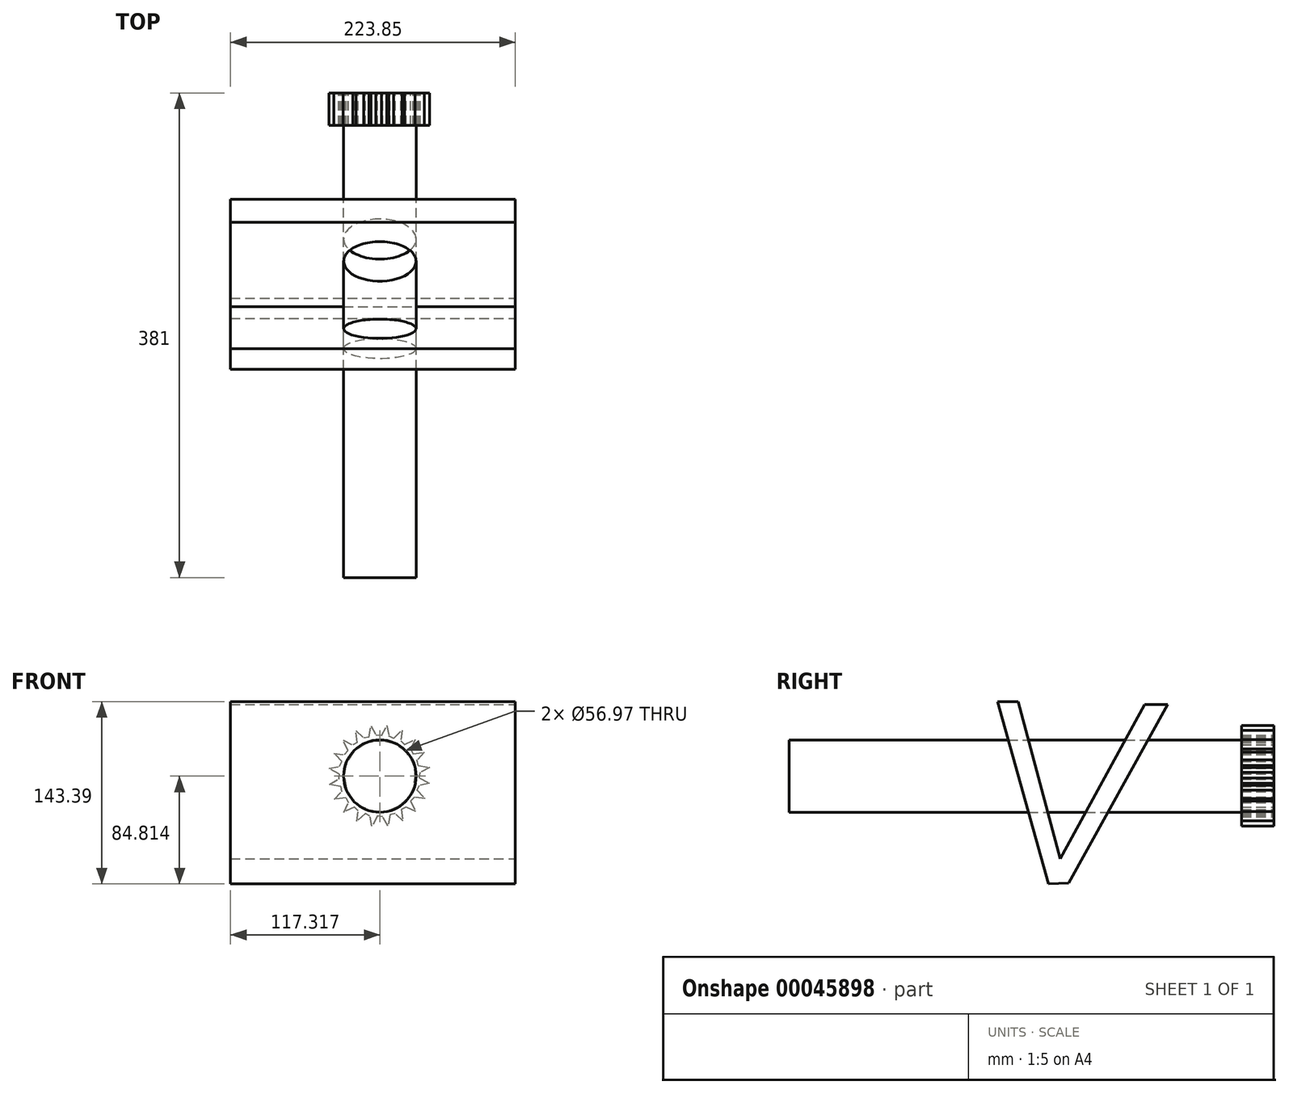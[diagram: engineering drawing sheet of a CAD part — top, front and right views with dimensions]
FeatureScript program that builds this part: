
annotation { "Feature Type Name" : "Feature", "Feature Type Description" : "" }
export const myFeature = defineFeature(function(context is Context, id is Id, definition is map)
    precondition{}
    {
        {
            var Q0;
            Q0=qCreatedBy(makeId("Front.planeOp"),FACE);
            var sketch = newSketch(context, id + "F0", { "sketchPlane" : qUnion([Q0])});
            skCircle(sketch, "E0", {"center": v(-106.53, 34.14) * mm, "radius": 28.48 * mm});
            skSolve(sketch);
        }
        {
            var Q0;
            Q0=makeQuery(id+"F0.imprint","IMPRINT",FACE,{"disambiguationData":[TD([[makeQuery(id+"F0.imprint","IMPRINT",EDGE,{"derivedFrom":sQuery(id+"F0.wireOp",EDGE,"E0")}),1.0]])]});
            extrude(context, id + "F1", {"entities" : qUnion([Q0]), "depth" : 381 * mm});
        }
        {
            var Q0;
            Q0=qCreatedBy(makeId("Right.planeOp"),FACE);
            var sketch = newSketch(context, id + "F2", { "sketchPlane" : qUnion([Q0])});
            skLineSegment(sketch, "E1", {"start": v(-83.69, 90.52) * mm, "end": v(-161.5, -50.05) * mm});
            skLineSegment(sketch, "E2", {"start": v(-83.69, 90.52) * mm, "end": v(-101.57, 90.52) * mm});
            skLineSegment(sketch, "E3", {"start": v(-101.57, 90.52) * mm, "end": v(-168.09, -30.9) * mm});
            skLineSegment(sketch, "E4", {"start": v(-168.09, -30.9) * mm, "end": v(-201.03, 92.72) * mm});
            skLineSegment(sketch, "E5", {"start": v(-201.03, 92.72) * mm, "end": v(-217.35, 92.72) * mm});
            skLineSegment(sketch, "E6", {"start": v(-217.35, 92.72) * mm, "end": v(-177.19, -50.67) * mm});
            skLineSegment(sketch, "E7", {"start": v(-177.19, -50.67) * mm, "end": v(-161.5, -50.05) * mm});
            skSolve(sketch);
        }
        {
            var Q0;
            Q0 = qSketchRegion(id + "F2", true);
            extrude(context, id + "F3", {"entities" : qUnion([Q0]), "oppositeDirection" : true, "depth" : 223.85 * mm});
        }
        {
            var Q0;
            Q0=makeQuery(id+"F1.opExtrude","SWEPT_BODY",BODY,{"disambiguationData":[OSD([sQuery(id+"F0.wireOp",EDGE,"E0")])]});
            var Q1;
            Q1=makeQuery(id+"F3.opExtrude","SWEPT_BODY",BODY,{"disambiguationData":[OSD([sQuery(id+"F2.wireOp",EDGE,"E1"),sQuery(id+"F2.wireOp",EDGE,"E2"),sQuery(id+"F2.wireOp",EDGE,"E3"),sQuery(id+"F2.wireOp",EDGE,"E4"),sQuery(id+"F2.wireOp",EDGE,"E5"),sQuery(id+"F2.wireOp",EDGE,"E6"),sQuery(id+"F2.wireOp",EDGE,"E7")])]});
            booleanBodies(context, id + "F4", {"operationType" : BooleanOperationType.SUBTRACTION, "tools" : qUnion([Q0]), "targets" : qUnion([Q1]), "keepTools" : true});
        }
        {
            var Q0;
            Q0=qCreatedBy(makeId("Front.planeOp"),FACE);
            var sketch = newSketch(context, id + "F5", { "sketchPlane" : qUnion([Q0])});
            skLineSegment(sketch, "E8", {"start": v(-115.19, 64.77) * mm, "end": v(-113.52, 73.75) * mm});
            skLineSegment(sketch, "E9", {"start": v(-113.52, 73.75) * mm, "end": v(-109.55, 66.44) * mm});
            skLineSegment(sketch, "E10.1.0", {"start": v(-101, 73.87) * mm, "end": v(-99.49, 65.69) * mm});
            skLineSegment(sketch, "E10.1.1", {"start": v(-105.37, 65.84) * mm, "end": v(-101, 73.87) * mm});
            skLineSegment(sketch, "E10.2.0", {"start": v(-89.07, 70.11) * mm, "end": v(-90.16, 61.86) * mm});
            skLineSegment(sketch, "E10.2.1", {"start": v(-95.7, 63.83) * mm, "end": v(-89.07, 70.11) * mm});
            skLineSegment(sketch, "E10.3.0", {"start": v(-78.88, 62.85) * mm, "end": v(-82.46, 55.35) * mm});
            skLineSegment(sketch, "E10.3.1", {"start": v(-87.13, 58.93) * mm, "end": v(-78.88, 62.85) * mm});
            skLineSegment(sketch, "E10.4.0", {"start": v(-71.43, 52.8) * mm, "end": v(-77.16, 46.77) * mm});
            skLineSegment(sketch, "E10.4.1", {"start": v(-80.5, 51.62) * mm, "end": v(-71.43, 52.8) * mm});
            skLineSegment(sketch, "E10.5.0", {"start": v(-67.46, 40.94) * mm, "end": v(-74.77, 36.97) * mm});
            skLineSegment(sketch, "E10.5.1", {"start": v(-76.44, 42.61) * mm, "end": v(-67.46, 40.94) * mm});
            skLineSegment(sketch, "E10.6.0", {"start": v(-67.34, 28.43) * mm, "end": v(-75.52, 26.91) * mm});
            skLineSegment(sketch, "E10.6.1", {"start": v(-75.37, 32.8) * mm, "end": v(-67.34, 28.43) * mm});
            skLineSegment(sketch, "E10.7.0", {"start": v(-71.1, 16.5) * mm, "end": v(-79.34, 17.58) * mm});
            skLineSegment(sketch, "E10.7.1", {"start": v(-77.38, 23.13) * mm, "end": v(-71.1, 16.5) * mm});
            skLineSegment(sketch, "E10.8.0", {"start": v(-78.35, 6.3) * mm, "end": v(-85.86, 9.89) * mm});
            skLineSegment(sketch, "E10.8.1", {"start": v(-82.28, 14.55) * mm, "end": v(-78.35, 6.3) * mm});
            skLineSegment(sketch, "E10.9.0", {"start": v(-88.4, -1.14) * mm, "end": v(-94.44, 4.58) * mm});
            skLineSegment(sketch, "E10.9.1", {"start": v(-89.6, 7.92) * mm, "end": v(-88.4, -1.14) * mm});
            skLineSegment(sketch, "E10.10.0", {"start": v(-100.27, -5.12) * mm, "end": v(-104.24, 2.2) * mm});
            skLineSegment(sketch, "E10.10.1", {"start": v(-98.6, 3.86) * mm, "end": v(-100.27, -5.12) * mm});
            skLineSegment(sketch, "E10.11.0", {"start": v(-112.78, -5.24) * mm, "end": v(-114.3, 2.94) * mm});
            skLineSegment(sketch, "E10.11.1", {"start": v(-108.41, 2.8) * mm, "end": v(-112.78, -5.24) * mm});
            skLineSegment(sketch, "E10.12.0", {"start": v(-124.71, -1.48) * mm, "end": v(-123.63, 6.77) * mm});
            skLineSegment(sketch, "E10.12.1", {"start": v(-118.08, 4.8) * mm, "end": v(-124.71, -1.48) * mm});
            skLineSegment(sketch, "E10.13.0", {"start": v(-134.9, 5.78) * mm, "end": v(-131.32, 13.29) * mm});
            skLineSegment(sketch, "E10.13.1", {"start": v(-126.65, 9.7) * mm, "end": v(-134.9, 5.78) * mm});
            skLineSegment(sketch, "E10.14.0", {"start": v(-142.35, 15.83) * mm, "end": v(-136.62, 21.86) * mm});
            skLineSegment(sketch, "E10.14.1", {"start": v(-133.3, 17.02) * mm, "end": v(-142.35, 15.83) * mm});
            skLineSegment(sketch, "E10.15.0", {"start": v(-146.33, 27.7) * mm, "end": v(-139.02, 31.66) * mm});
            skLineSegment(sketch, "E10.15.1", {"start": v(-137.34, 26.02) * mm, "end": v(-146.33, 27.7) * mm});
            skLineSegment(sketch, "E10.16.0", {"start": v(-146.44, 40.2) * mm, "end": v(-138.26, 41.72) * mm});
            skLineSegment(sketch, "E10.16.1", {"start": v(-138.42, 35.84) * mm, "end": v(-146.44, 40.2) * mm});
            skLineSegment(sketch, "E10.17.0", {"start": v(-142.69, 52.14) * mm, "end": v(-134.44, 51.05) * mm});
            skLineSegment(sketch, "E10.17.1", {"start": v(-136.4, 45.5) * mm, "end": v(-142.69, 52.14) * mm});
            skLineSegment(sketch, "E10.18.0", {"start": v(-135.43, 62.33) * mm, "end": v(-127.92, 58.74) * mm});
            skLineSegment(sketch, "E10.18.1", {"start": v(-131.5, 54.08) * mm, "end": v(-135.43, 62.33) * mm});
            skLineSegment(sketch, "E10.19.0", {"start": v(-125.38, 69.77) * mm, "end": v(-119.34, 64.05) * mm});
            skLineSegment(sketch, "E10.19.1", {"start": v(-124.2, 60.71) * mm, "end": v(-125.38, 69.77) * mm});
            skPoint(sketch, "E10.center", {"position": v(-106.9, 34.32) * mm});
            skLineSegment(sketch, "E10.anchor1", {"start": v(-106.9, 34.32) * mm, "end": v(-109.55, 66.44) * mm, "construction": true});
            skLineSegment(sketch, "E10.anchor2", {"start": v(-106.9, 34.32) * mm, "end": v(-119.34, 64.05) * mm, "construction": true});
            skLineSegment(sketch, "E11", {"start": v(-95.7, 63.83) * mm, "end": v(-99.49, 65.69) * mm});
            skLineSegment(sketch, "E12", {"start": v(-105.37, 65.84) * mm, "end": v(-109.55, 66.44) * mm});
            skLineSegment(sketch, "E13", {"start": v(-115.19, 64.77) * mm, "end": v(-119.34, 64.05) * mm});
            skLineSegment(sketch, "E14", {"start": v(-124.2, 60.71) * mm, "end": v(-127.92, 58.74) * mm});
            skLineSegment(sketch, "E15", {"start": v(-134.44, 51.05) * mm, "end": v(-131.5, 54.08) * mm});
            skLineSegment(sketch, "E16", {"start": v(-138.26, 41.72) * mm, "end": v(-136.4, 45.5) * mm});
            skLineSegment(sketch, "E17", {"start": v(-138.42, 35.84) * mm, "end": v(-139.02, 31.66) * mm});
            skLineSegment(sketch, "E18", {"start": v(-137.34, 26.02) * mm, "end": v(-136.62, 21.86) * mm});
            skLineSegment(sketch, "E19", {"start": v(-133.3, 17.02) * mm, "end": v(-131.32, 13.29) * mm});
            skLineSegment(sketch, "E20", {"start": v(-123.63, 6.77) * mm, "end": v(-126.65, 9.7) * mm});
            skLineSegment(sketch, "E21", {"start": v(-114.3, 2.94) * mm, "end": v(-118.08, 4.8) * mm});
            skLineSegment(sketch, "E22", {"start": v(-104.24, 2.2) * mm, "end": v(-108.41, 2.8) * mm});
            skLineSegment(sketch, "E23", {"start": v(-94.44, 4.58) * mm, "end": v(-98.6, 3.86) * mm});
            skLineSegment(sketch, "E24", {"start": v(-85.86, 9.89) * mm, "end": v(-89.6, 7.92) * mm});
            skLineSegment(sketch, "E25", {"start": v(-79.34, 17.58) * mm, "end": v(-82.28, 14.55) * mm});
            skLineSegment(sketch, "E26", {"start": v(-77.38, 23.13) * mm, "end": v(-75.52, 26.91) * mm});
            skLineSegment(sketch, "E27", {"start": v(-75.37, 32.8) * mm, "end": v(-74.77, 36.97) * mm});
            skLineSegment(sketch, "E28", {"start": v(-76.44, 42.61) * mm, "end": v(-77.16, 46.77) * mm});
            skLineSegment(sketch, "E29", {"start": v(-82.46, 55.35) * mm, "end": v(-80.5, 51.62) * mm});
            skLineSegment(sketch, "E30", {"start": v(-87.13, 58.93) * mm, "end": v(-90.16, 61.86) * mm});
            skSolve(sketch);
        }
        {
            var Q0;
            Q0 = qSketchRegion(id + "F5", true);
            extrude(context, id + "F6", {"entities" : qUnion([Q0]), "operationType" : NewBodyOperationType.ADD, "depth" : 25.4 * mm});
        }
    });
